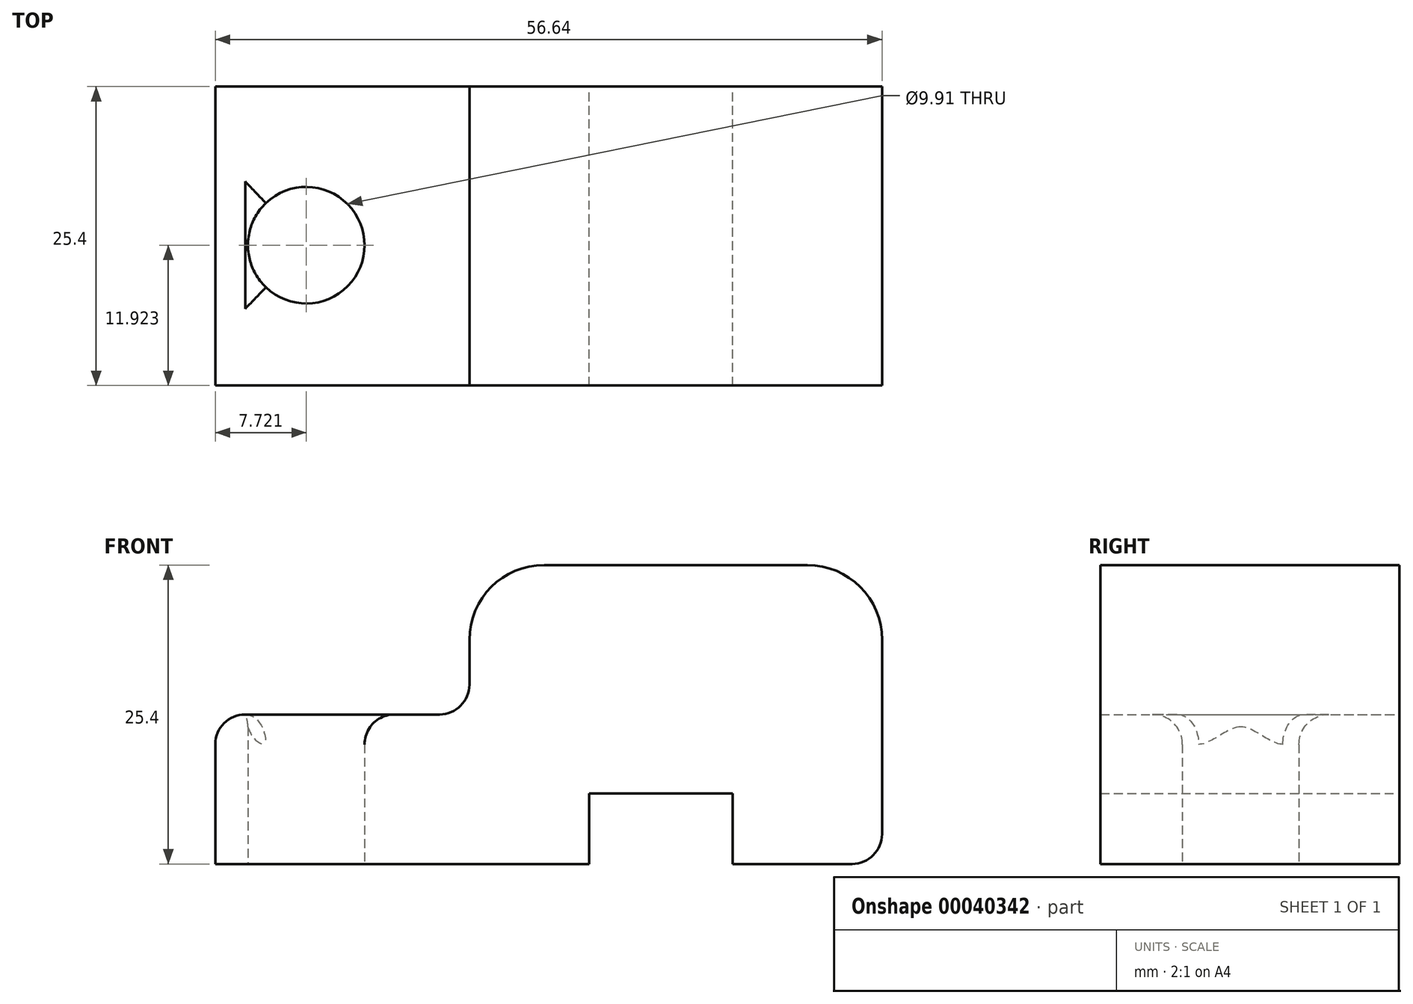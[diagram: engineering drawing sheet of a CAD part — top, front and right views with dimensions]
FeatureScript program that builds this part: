
annotation { "Feature Type Name" : "Feature", "Feature Type Description" : "" }
export const myFeature = defineFeature(function(context is Context, id is Id, definition is map)
    precondition{}
    {
        {
            var Q0;
            Q0=qCreatedBy(makeId("Front.planeOp"),FACE);
            var sketch = newSketch(context, id + "F0", { "sketchPlane" : qUnion([Q0])});
            skLineSegment(sketch, "E0", {"start": v(-2.54, 0) * mm, "end": v(-12.7, 0) * mm});
            skLineSegment(sketch, "E1", {"start": v(-12.7, 0) * mm, "end": v(-12.7, 6) * mm});
            skLineSegment(sketch, "E2", {"start": v(-12.7, 6) * mm, "end": v(-24.9, 6) * mm});
            skLineSegment(sketch, "E3", {"start": v(-24.9, 6) * mm, "end": v(-24.9, 0) * mm});
            skLineSegment(sketch, "E4", {"start": v(-24.9, 0) * mm, "end": v(-56.64, 0) * mm});
            skLineSegment(sketch, "E5", {"start": v(-56.64, 0) * mm, "end": v(-56.64, 10.16) * mm});
            skLineSegment(sketch, "E6", {"start": v(-54.1, 12.7) * mm, "end": v(-37.6, 12.7) * mm});
            skLineSegment(sketch, "E7", {"start": v(-35.05, 15.24) * mm, "end": v(-35.05, 19.05) * mm});
            skLineSegment(sketch, "E8", {"start": v(-28.7, 25.4) * mm, "end": v(-6.35, 25.4) * mm});
            skLineSegment(sketch, "E9", {"start": v(0, 19.05) * mm, "end": v(0, 2.54) * mm});
            skPoint(sketch, "E10.visualSharp", {"position": v(0, 25.4) * mm});
            skArc(sketch, "E10.filletArc", {"start": v(0, 19.05) * mm, "mid": v(-1.86, 23.54) * mm, "end": v(-6.35, 25.4) * mm});
            skPoint(sketch, "E11.visualSharp", {"position": v(-35.05, 25.4) * mm});
            skArc(sketch, "E11.filletArc", {"start": v(-28.7, 25.4) * mm, "mid": v(-33.2, 23.54) * mm, "end": v(-35.05, 19.05) * mm});
            skPoint(sketch, "E12.visualSharp", {"position": v(-56.64, 12.7) * mm});
            skArc(sketch, "E12.filletArc", {"start": v(-54.1, 12.7) * mm, "mid": v(-55.9, 11.96) * mm, "end": v(-56.64, 10.16) * mm});
            skPoint(sketch, "E13.visualSharp", {"position": v(-35.05, 12.7) * mm});
            skArc(sketch, "E13.filletArc", {"start": v(-37.6, 12.7) * mm, "mid": v(-35.8, 13.44) * mm, "end": v(-35.05, 15.24) * mm});
            skPoint(sketch, "E14.visualSharp", {"position": v(0, 0) * mm});
            skArc(sketch, "E14.filletArc", {"start": v(-2.54, 0) * mm, "mid": v(-0.74, 0.74) * mm, "end": v(0, 2.54) * mm});
            skSolve(sketch);
        }
        {
            var Q0;
            Q0=makeQuery(id+"F0.imprint","IMPRINT",FACE,{"disambiguationData":[TD([[makeQuery(id+"F0.imprint","IMPRINT",EDGE,{"derivedFrom":sQuery(id+"F0.wireOp",EDGE,"E0")}),-1.0]])]});
            extrude(context, id + "F1", {"entities" : qUnion([Q0]), "depth" : 25.4 * mm});
        }
        {
            var Q0;
            Q0=makeQuery(id+"F1.opExtrude","SWEPT_FACE",FACE,{"disambiguationData":[OSD([sQuery(id+"F0.wireOp",EDGE,"E4")])]});
            var sketch = newSketch(context, id + "F2", { "sketchPlane" : qUnion([Q0])});
            skPoint(sketch, "E15.centerSnap0", {"position": v(-40.77, 25.4) * mm});
            skPoint(sketch, "E15.centerSnap1", {"position": v(-56.64, 12.7) * mm});
            skCircle(sketch, "E16", {"center": v(-48.92, 13.48) * mm, "radius": 4.95 * mm});
            skPoint(sketch, "E16.first.point", {"position": v(-53.81, 12.7) * mm});
            skPoint(sketch, "E16.second.point", {"position": v(-43.98, 13.88) * mm});
            skPoint(sketch, "E16.third.point", {"position": v(-47.6, 8.7) * mm});
            skSolve(sketch);
        }
        {
            var Q0;
            Q0=makeQuery(id+"F2.imprint","IMPRINT",FACE,{"disambiguationData":[TD([[makeQuery(id+"F2.imprint","IMPRINT",EDGE,{"derivedFrom":sQuery(id+"F2.wireOp",EDGE,"E16")}),1.0]])]});
            extrude(context, id + "F3", {"entities" : qUnion([Q0]), "operationType" : NewBodyOperationType.REMOVE, "oppositeDirection" : true, "depth" : 25.4 * mm});
        }
        {
            var Q0;
            Q0=makeQuery(id+"F3.boolean.opBoolean","INTERSECT",EDGE,{"derivedFrom":[makeQuery(id+"F1.opExtrude","SWEPT_FACE",FACE,{"disambiguationData":[OSD([sQuery(id+"F0.wireOp",EDGE,"E6")])]}),makeQuery(id+"F3.opExtrude","SWEPT_FACE",FACE,{"disambiguationData":[OSD([sQuery(id+"F2.wireOp",EDGE,"E16")])]})]});
            fillet(context, id + "F4", {"entities" : qUnion([Q0]), "radius" : 2.54 * mm, "tangentPropagation" : true, "allowEdgeOverflow" : false});
        }
    });
